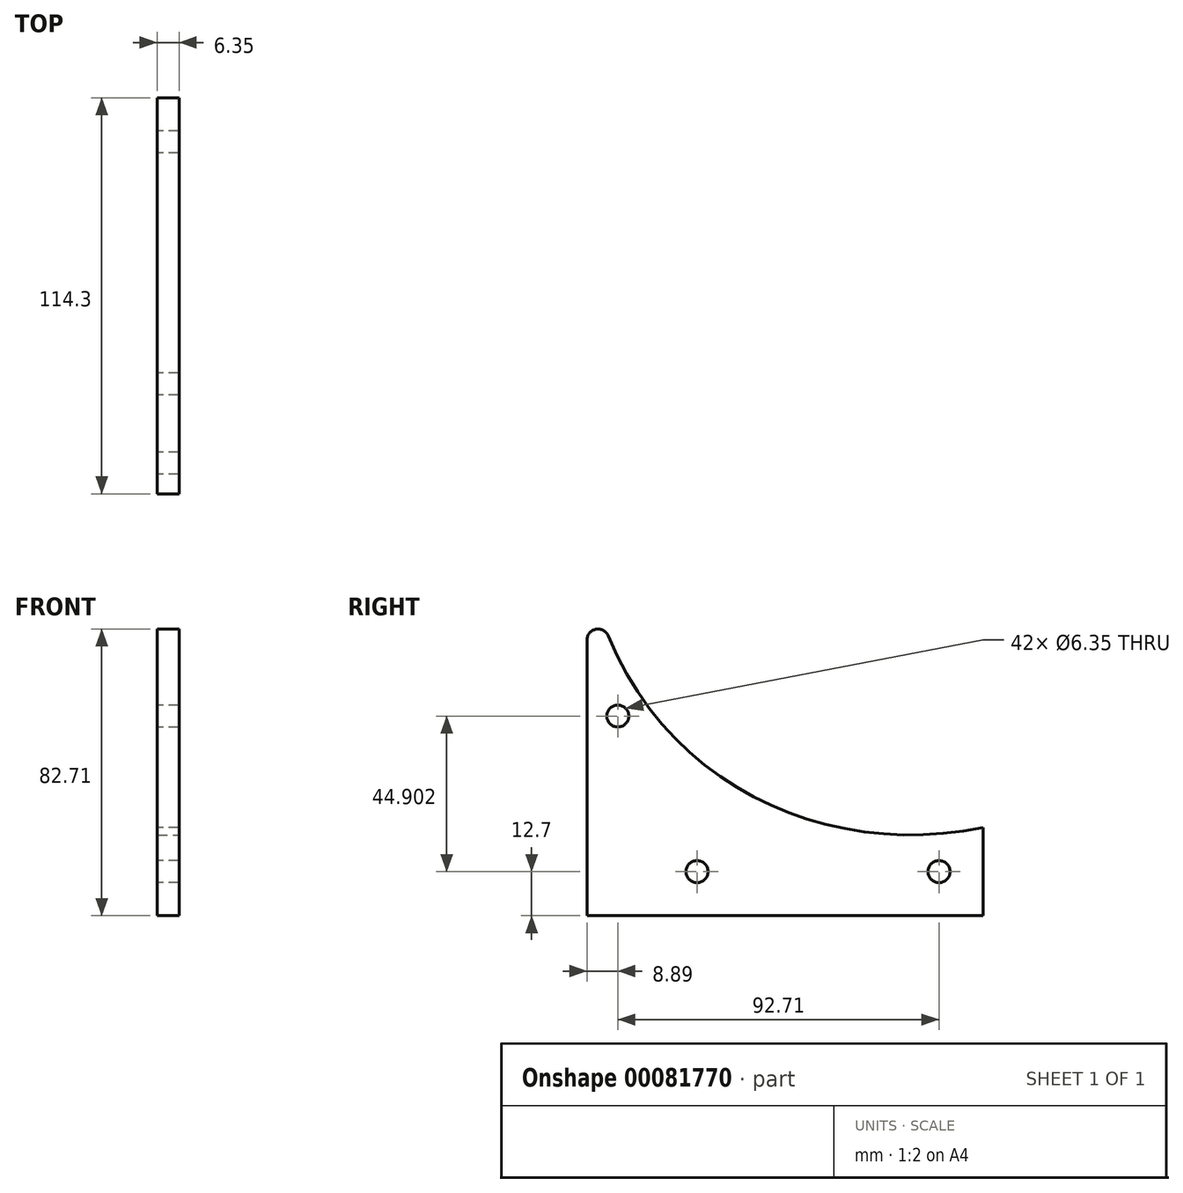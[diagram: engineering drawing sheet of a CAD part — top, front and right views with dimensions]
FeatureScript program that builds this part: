
annotation { "Feature Type Name" : "Feature", "Feature Type Description" : "" }
export const myFeature = defineFeature(function(context is Context, id is Id, definition is map)
    precondition{}
    {
        {
            var Q0;
            Q0=qCreatedBy(makeId("Right.planeOp"),FACE);
            var sketch = newSketch(context, id + "F0", { "sketchPlane" : qUnion([Q0])});
            skLineSegment(sketch, "E0", {"start": v(0, 0) * mm, "end": v(0, 79.53) * mm});
            skLineSegment(sketch, "E1", {"start": v(114.3, 0) * mm, "end": v(114.3, 25.4) * mm});
            skFitSpline(sketch, "E2", {"points": [v(0, 101.6) * mm, v(114.3, 25.4) * mm], "startDerivative": vector(33.02, -176.63) * mm, "endDerivative": vector(151.14, 30.85) * mm});
            skLineSegment(sketch, "E3", {"start": v(0, 0) * mm, "end": v(114.3, 0) * mm});
            skArc(sketch, "E4.filletArc", {"start": v(6.11, 80.74) * mm, "mid": v(2.56, 82.65) * mm, "end": v(0, 79.53) * mm});
            skLineSegment(sketch, "E5", {"start": v(114.3, 12.7) * mm, "end": v(0, 12.7) * mm, "construction": true});
            skCircle(sketch, "E6", {"center": v(31.75, 12.7) * mm, "radius": 3.18 * mm});
            skCircle(sketch, "E7", {"center": v(101.6, 12.7) * mm, "radius": 3.18 * mm});
            skLineSegment(sketch, "E8", {"start": v(8.9, 0) * mm, "end": v(8.9, 97.6) * mm, "construction": true});
            skCircle(sketch, "E9", {"center": v(8.9, 57.6) * mm, "radius": 3.18 * mm});
            skSolve(sketch);
        }
        {
            var Q0;
            Q0 = qSketchRegion(id + "F0", true);
            extrude(context, id + "F1", {"entities" : qUnion([Q0]), "depth" : 6.35 * mm});
        }
    });
